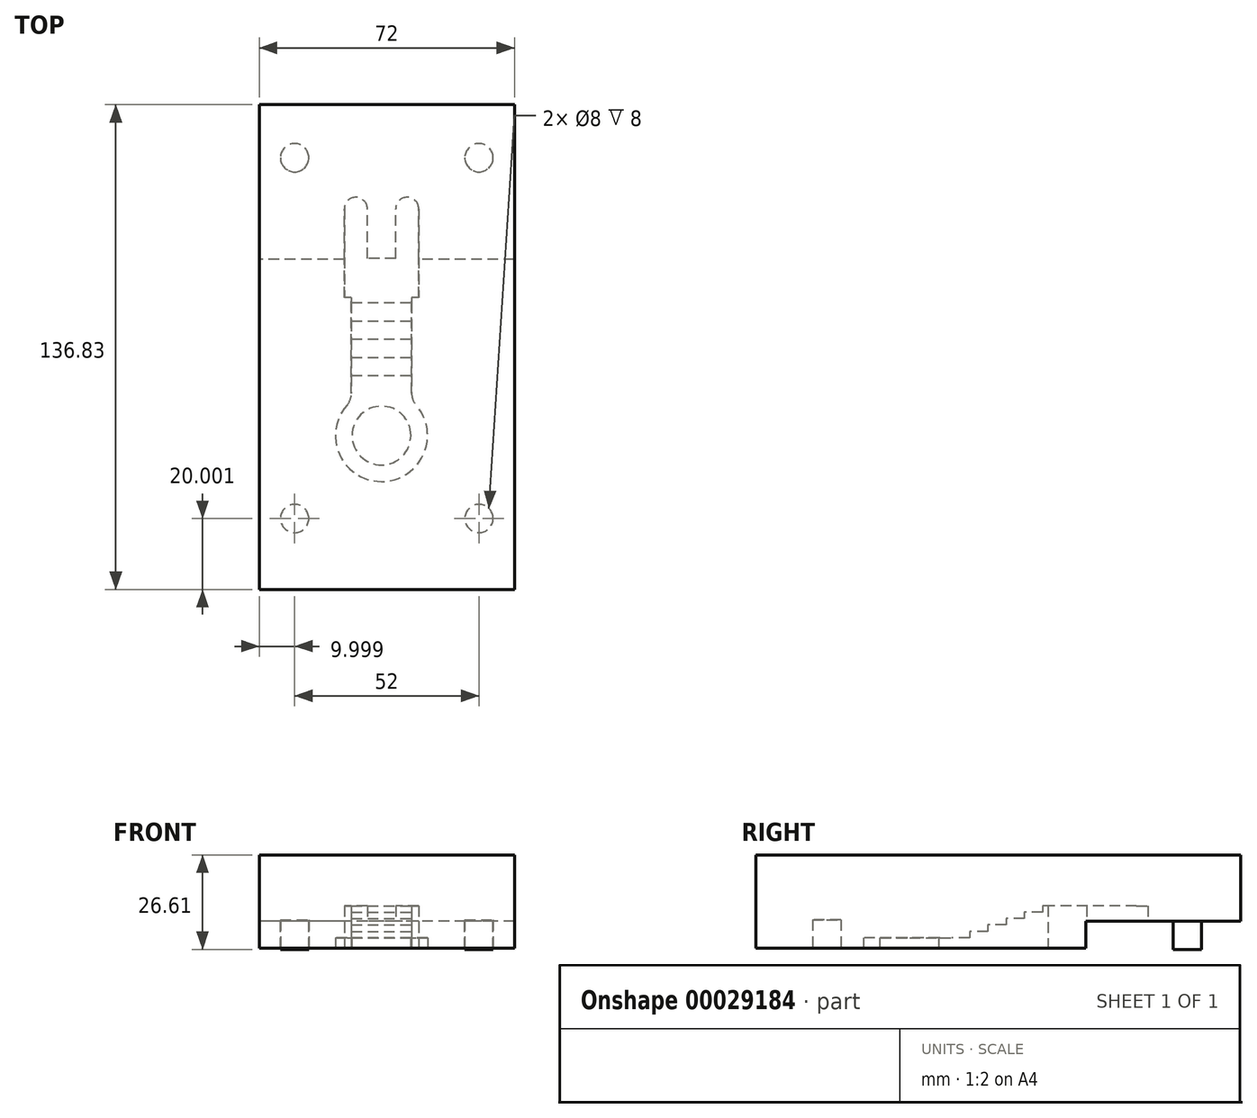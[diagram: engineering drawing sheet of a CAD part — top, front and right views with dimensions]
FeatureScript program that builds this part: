
annotation { "Feature Type Name" : "Feature", "Feature Type Description" : "" }
export const myFeature = defineFeature(function(context is Context, id is Id, definition is map)
    precondition{}
    {
        {
            var Q0;
            Q0=qCreatedBy(makeId("Top.planeOp"),FACE);
            var sketch = newSketch(context, id + "F0", { "sketchPlane" : qUnion([Q0])});
            skLineSegment(sketch, "E0.top", {"start": v(-85.13, 11.8) * mm, "end": v(-83.13, 11.8) * mm});
            skLineSegment(sketch, "E0.left", {"start": v(-85.13, 36.8) * mm, "end": v(-85.13, 11.8) * mm});
            skLineSegment(sketch, "E0.right", {"start": v(-64.13, 36.8) * mm, "end": v(-64.13, 11.8) * mm});
            skLineSegment(sketch, "E1.top", {"start": v(-78.63, 22.8) * mm, "end": v(-70.63, 22.8) * mm});
            skLineSegment(sketch, "E1.left", {"start": v(-78.63, 36.8) * mm, "end": v(-78.63, 22.8) * mm});
            skLineSegment(sketch, "E1.right", {"start": v(-70.63, 36.8) * mm, "end": v(-70.63, 22.8) * mm});
            skLineSegment(sketch, "E2.left", {"start": v(-83.13, 11.8) * mm, "end": v(-83.13, -15.3) * mm});
            skLineSegment(sketch, "E2.right", {"start": v(-66.13, 11.8) * mm, "end": v(-66.13, -15.3) * mm});
            skArc(sketch, "E3", {"start": v(-84.38, -18.6) * mm, "mid": v(-74.63, -40.2) * mm, "end": v(-64.88, -18.6) * mm});
            skLineSegment(sketch, "E4", {"start": v(-74.63, 22.8) * mm, "end": v(-74.63, -62.63) * mm, "construction": true});
            skPoint(sketch, "E5.visualSharp", {"position": v(-66.13, -17.37) * mm});
            skArc(sketch, "E5.filletArc", {"start": v(-66.13, -15.3) * mm, "mid": v(-65.8, -17.07) * mm, "end": v(-64.88, -18.6) * mm});
            skPoint(sketch, "E6.visualSharp", {"position": v(-83.13, -17.37) * mm});
            skArc(sketch, "E6.filletArc", {"start": v(-84.38, -18.6) * mm, "mid": v(-83.45, -17.07) * mm, "end": v(-83.13, -15.3) * mm});
            skPoint(sketch, "E7.visualSharp", {"position": v(-64.13, 11.8) * mm});
            skLineSegment(sketch, "E7.filletArc", {"start": v(-64.13, 11.8) * mm, "end": v(-64.13, 11.8) * mm});
            skPoint(sketch, "E8.visualSharp", {"position": v(-85.13, 11.8) * mm});
            skLineSegment(sketch, "E8.filletArc", {"start": v(-85.13, 11.8) * mm, "end": v(-85.13, 11.8) * mm});
            skLineSegment(sketch, "E9.trimOffspring", {"start": v(-66.13, 11.8) * mm, "end": v(-64.13, 11.8) * mm});
            skPoint(sketch, "E10.visualSharp", {"position": v(-83.13, 11.8) * mm});
            skLineSegment(sketch, "E10.filletArc", {"start": v(-83.13, 11.8) * mm, "end": v(-83.13, 11.8) * mm});
            skPoint(sketch, "E11.visualSharp", {"position": v(-66.13, 11.8) * mm});
            skLineSegment(sketch, "E11.filletArc", {"start": v(-66.13, 11.8) * mm, "end": v(-66.13, 11.8) * mm});
            skCircle(sketch, "E12", {"center": v(-74.63, -27.2) * mm, "radius": 6.75 * mm});
            skArc(sketch, "E13", {"start": v(-78.63, 36.8) * mm, "mid": v(-81.88, 40.05) * mm, "end": v(-85.13, 36.8) * mm});
            skArc(sketch, "E14", {"start": v(-64.13, 36.8) * mm, "mid": v(-67.38, 40.05) * mm, "end": v(-70.63, 36.8) * mm});
            skSolve(sketch);
        }
        {
            var Q0;
            Q0=makeQuery(id+"F0.imprint","IMPRINT",FACE,{"disambiguationData":[TD([[makeQuery(id+"F0.imprint","IMPRINT",EDGE,{"derivedFrom":sQuery(id+"F0.wireOp",EDGE,"E12")}),1.0]])]});
            var Q1;
            Q1=makeQuery(id+"F0.imprint","IMPRINT",FACE,{"disambiguationData":[TD([[makeQuery(id+"F0.imprint","IMPRINT",EDGE,{"derivedFrom":sQuery(id+"F0.wireOp",EDGE,"E0.top")}),1.0]])]});
            extrude(context, id + "F1", {"entities" : qUnion([Q0, Q1]), "depth" : 18 * mm});
        }
        {
            var Q0;
            Q0=qCreatedBy(makeId("Right.planeOp"),FACE);
            var sketch = newSketch(context, id + "F2", { "sketchPlane" : qUnion([Q0])});
            skLineSegment(sketch, "E15", {"start": v(-40.29, 25.83) * mm, "end": v(15.45, 25.83) * mm});
            skLineSegment(sketch, "E16", {"start": v(15.45, 25.83) * mm, "end": v(15.45, 18) * mm});
            skLineSegment(sketch, "E17", {"start": v(-10.3, 9) * mm, "end": v(-41.5, 9) * mm});
            skLineSegment(sketch, "E18", {"start": v(-41.5, 9) * mm, "end": v(-40.29, 25.83) * mm});
            skLineSegment(sketch, "E19", {"start": v(15.45, 18) * mm, "end": v(10.3, 18) * mm});
            skLineSegment(sketch, "E20", {"start": v(10.3, 18) * mm, "end": v(10.3, 16.2) * mm});
            skLineSegment(sketch, "E21", {"start": v(10.3, 16.2) * mm, "end": v(5.15, 16.2) * mm});
            skLineSegment(sketch, "E22", {"start": v(5.15, 16.2) * mm, "end": v(5.15, 14.4) * mm});
            skLineSegment(sketch, "E23", {"start": v(5.15, 14.4) * mm, "end": v(0, 14.4) * mm});
            skLineSegment(sketch, "E24", {"start": v(0, 14.4) * mm, "end": v(0, 12.6) * mm});
            skLineSegment(sketch, "E25", {"start": v(0, 12.6) * mm, "end": v(-5.15, 12.6) * mm});
            skLineSegment(sketch, "E26", {"start": v(-5.15, 12.6) * mm, "end": v(-5.15, 10.8) * mm});
            skLineSegment(sketch, "E27", {"start": v(-5.15, 10.8) * mm, "end": v(-10.3, 10.8) * mm});
            skLineSegment(sketch, "E28", {"start": v(-10.3, 10.8) * mm, "end": v(-10.3, 9) * mm});
            skSolve(sketch);
        }
        {
            var Q0;
            Q0=qSketchRegion(id+"F2",true);
            extrude(context, id + "F3", {"entities" : qUnion([Q0]), "operationType" : NewBodyOperationType.REMOVE, "oppositeDirection" : true, "depth" : 125 * mm});
        }
        {
            var Q0;
            Q0=makeQuery(id+"F3.boolean.opBoolean","COPY",FACE,{"derivedFrom":makeQuery(id+"F3.opExtrude","SWEPT_FACE",FACE,{"disambiguationData":[OSD([sQuery(id+"F2.wireOp",EDGE,"E17")])]})});
            var sketch = newSketch(context, id + "F4", { "sketchPlane" : qUnion([Q0])});
            skCircle(sketch, "E29", {"center": v(-74.63, -27.2) * mm, "radius": 8.3 * mm});
            skSolve(sketch);
        }
        {
            var Q0;
            Q0=qSketchRegion(id+"F4",true);
            extrude(context, id + "F5", {"entities" : qUnion([Q0]), "operationType" : NewBodyOperationType.REMOVE, "oppositeDirection" : true, "depth" : 3 * mm});
        }
        {
            var Q0;
            Q0=makeQuery(id+"F1.opExtrude","SWEPT_FACE",FACE,{"disambiguationData":[OSD([sQuery(id+"F0.wireOp",EDGE,"E0.right")])]});
            var sketch = newSketch(context, id + "F6", { "sketchPlane" : qUnion([Q0])});
            skCircle(sketch, "E30", {"center": v(30.8, 6) * mm, "radius": 2.5 * mm});
            skSolve(sketch);
        }
        {
            var Q0;
            Q0=makeQuery(id+"F1.opExtrude","SWEPT_FACE",FACE,{"disambiguationData":[OSD([sQuery(id+"F0.wireOp",EDGE,"E0.right")])]});
            var sketch = newSketch(context, id + "F7", { "sketchPlane" : qUnion([Q0])});
            skLineSegment(sketch, "E31", {"start": v(22.77, 0) * mm, "end": v(12.77, 0) * mm, "construction": true});
            skLineSegment(sketch, "E32", {"start": v(22.77, 0) * mm, "end": v(22.77, 17.98) * mm, "construction": true});
            skLineSegment(sketch, "E33", {"start": v(22.77, 17.98) * mm, "end": v(15.77, 17.98) * mm, "construction": true});
            skLineSegment(sketch, "E34", {"start": v(9.68, 20.3) * mm, "end": v(9.22, -2.99) * mm});
            skLineSegment(sketch, "E35", {"start": v(9.22, -2.99) * mm, "end": v(12.1, -2.99) * mm});
            skLineSegment(sketch, "E36", {"start": v(12.1, -2.99) * mm, "end": v(12.77, 0) * mm});
            skLineSegment(sketch, "E37", {"start": v(9.68, 20.3) * mm, "end": v(16.08, 19.87) * mm});
            skLineSegment(sketch, "E38", {"start": v(12.77, 0) * mm, "end": v(16.08, 19.87) * mm});
            skSolve(sketch);
        }
        {
            var Q0;
            Q0=makeQuery(id+"F1.opExtrude","SWEPT_FACE",FACE,{"disambiguationData":[OSD([sQuery(id+"F0.wireOp",EDGE,"E0.left")])]});
            var sketch = newSketch(context, id + "F8", { "sketchPlane" : qUnion([Q0])});
            skLineSegment(sketch, "E39", {"start": v(-12.8, 0) * mm, "end": v(-15.71, 18) * mm});
            skLineSegment(sketch, "E40", {"start": v(-15.71, 18) * mm, "end": v(-12.42, 21.29) * mm});
            skLineSegment(sketch, "E41", {"start": v(-12.42, 21.29) * mm, "end": v(-9.36, 20.22) * mm});
            skLineSegment(sketch, "E42", {"start": v(-9.36, 20.22) * mm, "end": v(-8.88, -2.86) * mm});
            skLineSegment(sketch, "E43", {"start": v(-8.88, -2.86) * mm, "end": v(-12.32, -2.93) * mm});
            skLineSegment(sketch, "E44", {"start": v(-12.32, -2.93) * mm, "end": v(-12.8, 0) * mm});
            skSolve(sketch);
        }
        {
            var Q0;
            Q0=makeQuery(id+"F1.opExtrude","SWEPT_FACE",FACE,{"disambiguationData":[OSD([sQuery(id+"F0.wireOp",EDGE,"E0.right")])]});
            var sketch = newSketch(context, id + "F9", { "sketchPlane" : qUnion([Q0])});
            skLineSegment(sketch, "E45", {"start": v(-70.63, 6) * mm, "end": v(-70.63, 32.33) * mm});
            skLineSegment(sketch, "E46", {"start": v(-70.63, 32.33) * mm, "end": v(66.2, 32.33) * mm});
            skLineSegment(sketch, "E47", {"start": v(66.2, 32.33) * mm, "end": v(66.2, 13.72) * mm});
            skLineSegment(sketch, "E48", {"start": v(66.2, 13.72) * mm, "end": v(66.2, -16.86) * mm});
            skLineSegment(sketch, "E49", {"start": v(66.2, -16.86) * mm, "end": v(-70.63, -16.86) * mm});
            skLineSegment(sketch, "E50", {"start": v(-70.63, -16.86) * mm, "end": v(-70.63, 6) * mm});
            skLineSegment(sketch, "E51", {"start": v(-70.63, 6) * mm, "end": v(22.49, 6) * mm});
            skLineSegment(sketch, "E52", {"start": v(22.49, 13.72) * mm, "end": v(22.49, 6) * mm});
            skLineSegment(sketch, "E53", {"start": v(22.49, 13.72) * mm, "end": v(66.2, 13.72) * mm});
            skSolve(sketch);
        }
        {
            var Q0;
            {var subQ10=sQuery(id+"F9.wireOp",EDGE,"E45");Q0=makeQuery(id+"F9.imprint","IMPRINT",FACE,{"disambiguationData":[TD([[makeQuery(id+"F9.imprint","IMPRINT",EDGE,{"derivedFrom":subQ10}),-1.0]])]});}
            var Q1;
            {var subQ9=sQuery(id+"F9.wireOp",EDGE,"E52");Q1=makeQuery(id+"F9.imprint","IMPRINT",FACE,{"disambiguationData":[TD([[makeQuery(id+"F9.imprint","IMPRINT",EDGE,{"derivedFrom":subQ9}),-1.0]])]});}
            extrude(context, id + "F10", {"entities" : qUnion([Q0, Q1]), "depth" : 27 * mm, "hasSecondDirection" : true, "secondDirectionOppositeDirection" : true, "secondDirectionDepth" : 45 * mm});
        }
        {
            var Q0;
            Q0=makeQuery(id+"F10.opExtrude","SWEPT_FACE",FACE,{"disambiguationData":[OSD([sQuery(id+"F9.wireOp",EDGE,"E51")])]});
            var sketch = newSketch(context, id + "F11", { "sketchPlane" : qUnion([Q0])});
            skCircle(sketch, "E54", {"center": v(-99.13, 50.63) * mm, "radius": 4 * mm});
            skCircle(sketch, "E55", {"center": v(-47.13, 50.63) * mm, "radius": 4 * mm});
            skLineSegment(sketch, "E56", {"start": v(-99.13, 50.63) * mm, "end": v(-47.13, 50.63) * mm, "construction": true});
            skSolve(sketch);
        }
        {
            var Q0;
            Q0=makeQuery(id+"F10.opExtrude","SWEPT_FACE",FACE,{"disambiguationData":[OSD([sQuery(id+"F9.wireOp",EDGE,"E53")])]});
            var sketch = newSketch(context, id + "F12", { "sketchPlane" : qUnion([Q0])});
            skCircle(sketch, "E57", {"center": v(-99.13, -51.2) * mm, "radius": 4 * mm});
            skCircle(sketch, "E58", {"center": v(-47.13, -51.2) * mm, "radius": 4 * mm});
            skLineSegment(sketch, "E59", {"start": v(-99.13, -51.2) * mm, "end": v(-47.13, -51.2) * mm, "construction": true});
            skSolve(sketch);
        }
        {
            var Q0;
            Q0=makeQuery(id+"F12.imprint","IMPRINT",FACE,{"disambiguationData":[TD([[makeQuery(id+"F12.imprint","IMPRINT",EDGE,{"derivedFrom":sQuery(id+"F12.wireOp",EDGE,"E57")}),1.0]])]});
            var Q1;
            Q1=makeQuery(id+"F12.imprint","IMPRINT",FACE,{"disambiguationData":[TD([[makeQuery(id+"F12.imprint","IMPRINT",EDGE,{"derivedFrom":sQuery(id+"F12.wireOp",EDGE,"E58")}),1.0]])]});
            extrude(context, id + "F13", {"entities" : qUnion([Q0, Q1]), "operationType" : NewBodyOperationType.ADD, "depth" : 8 * mm});
        }
        {
            var Q0;
            Q0=makeQuery(id+"F11.imprint","IMPRINT",FACE,{"disambiguationData":[TD([[makeQuery(id+"F11.imprint","IMPRINT",EDGE,{"derivedFrom":sQuery(id+"F11.wireOp",EDGE,"E54")}),1.0]])]});
            var Q1;
            Q1=makeQuery(id+"F11.imprint","IMPRINT",FACE,{"disambiguationData":[TD([[makeQuery(id+"F11.imprint","IMPRINT",EDGE,{"derivedFrom":sQuery(id+"F11.wireOp",EDGE,"E55")}),1.0]])]});
            extrude(context, id + "F14", {"entities" : qUnion([Q0, Q1]), "operationType" : NewBodyOperationType.REMOVE, "oppositeDirection" : true, "depth" : 8 * mm});
        }
        {
            var Q0;
            Q0=makeQuery(id+"F1.opExtrude","SWEPT_BODY",BODY,{"disambiguationData":[OSD([sQuery(id+"F0.wireOp",EDGE,"E0.bottom"),sQuery(id+"F0.wireOp",EDGE,"E0.top"),sQuery(id+"F0.wireOp",EDGE,"E0.left"),sQuery(id+"F0.wireOp",EDGE,"E0.right"),sQuery(id+"F0.wireOp",EDGE,"E1.top"),sQuery(id+"F0.wireOp",EDGE,"E1.left"),sQuery(id+"F0.wireOp",EDGE,"E1.right"),sQuery(id+"F0.wireOp",EDGE,"3b6ef628-da63-4f4e-a1c5-ea05c0a2540d.trimOffspring"),sQuery(id+"F0.wireOp",EDGE,"E2.left"),sQuery(id+"F0.wireOp",EDGE,"E2.right"),sQuery(id+"F0.wireOp",EDGE,"E3"),sQuery(id+"F0.wireOp",EDGE,"E5.filletArc"),sQuery(id+"F0.wireOp",EDGE,"E6.filletArc"),sQuery(id+"F0.wireOp",EDGE,"E9.trimOffspring")])]});
            var Q1;
            Q1=makeQuery(id+"F10.opExtrude","SWEPT_BODY",BODY,{"disambiguationData":[OSD([sQuery(id+"F9.wireOp",EDGE,"a7e27d74-994a-4891-aaa3-0980bfbdc30e"),sQuery(id+"F9.wireOp",EDGE,"fb911d7a-c046-4048-9a62-8b9bea53e43f"),sQuery(id+"F9.wireOp",EDGE,"E45"),sQuery(id+"F9.wireOp",EDGE,"E46"),sQuery(id+"F9.wireOp",EDGE,"E47"),sQuery(id+"F9.wireOp",EDGE,"ea3ffea4-3806-48fb-9a5a-532117da88c0")])]});
            booleanBodies(context, id + "F15", {"operationType" : BooleanOperationType.SUBTRACTION, "tools" : qUnion([Q0]), "targets" : qUnion([Q1])});
        }
    });
